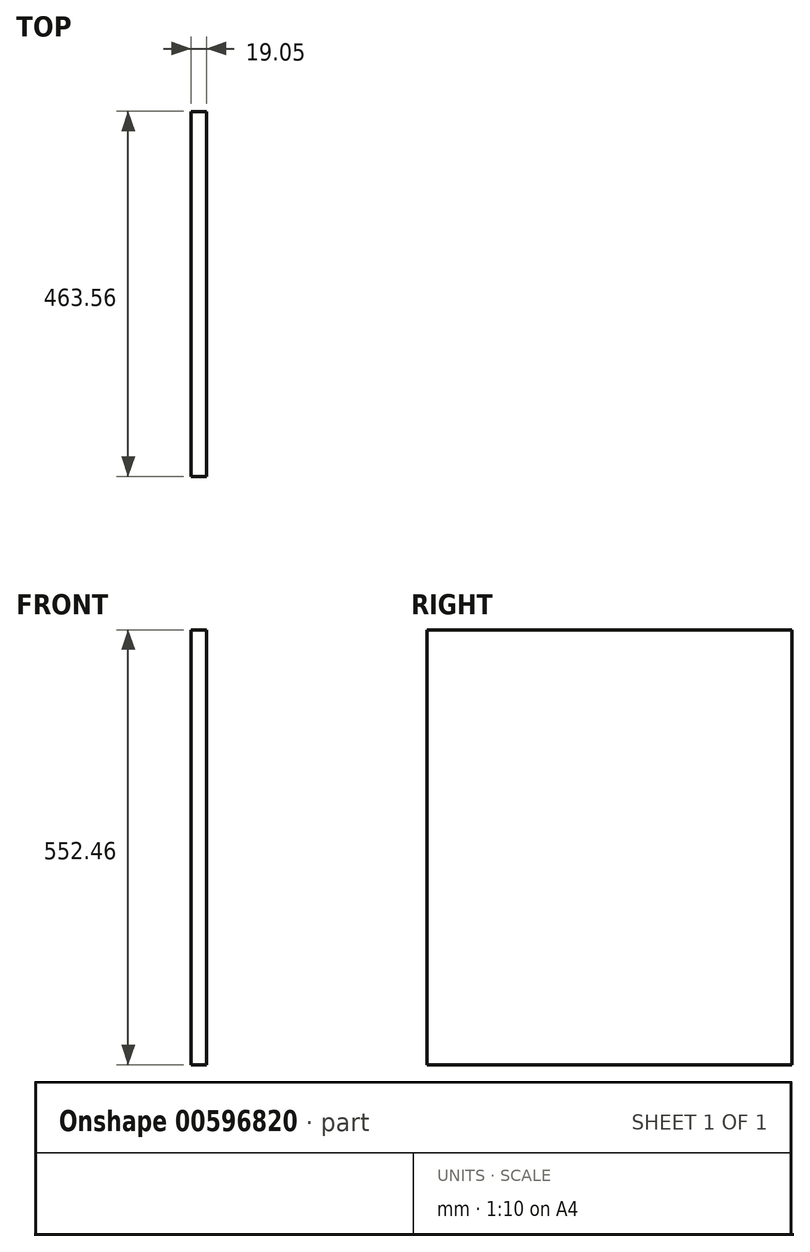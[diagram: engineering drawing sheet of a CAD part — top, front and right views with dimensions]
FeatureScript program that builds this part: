
annotation { "Feature Type Name" : "Feature", "Feature Type Description" : "" }
export const myFeature = defineFeature(function(context is Context, id is Id, definition is map)
    precondition{}
    {
        {
            var Q0;
            Q0=qCreatedBy(makeId("Right.planeOp"),FACE);
            var sketch = newSketch(context, id + "F0", { "sketchPlane" : qUnion([Q0])});
            skLineSegment(sketch, "E0.bottom", {"start": v(231.78, 276.23) * mm, "end": v(-231.77, 276.23) * mm});
            skLineSegment(sketch, "E0.top", {"start": v(231.78, -276.23) * mm, "end": v(-231.78, -276.23) * mm});
            skLineSegment(sketch, "E0.left", {"start": v(231.78, 276.23) * mm, "end": v(231.78, -276.23) * mm});
            skLineSegment(sketch, "E0.right", {"start": v(-231.77, 276.23) * mm, "end": v(-231.78, -276.23) * mm});
            skPoint(sketch, "E0.middle", {"position": v(0, 0) * mm});
            skSolve(sketch);
        }
        {
            var Q0;
            Q0=makeQuery(id+"F0.imprint","IMPRINT",FACE,{"disambiguationData":[TD([[makeQuery(id+"F0.imprint","IMPRINT",EDGE,{"derivedFrom":sQuery(id+"F0.wireOp",EDGE,"E0.bottom")}),1.0]])]});
            extrude(context, id + "F1", {"entities" : qUnion([Q0]), "depth" : 19.05 * mm, "offsetDistance" : 25.4 * mm});
        }
    });
